# Revit family: 4_CFS494NVNA+TCF5841P+TES47MR+TH343R+HP430-7
name_source: partatom
category: 衛生器具
units: mm (PartAtom-declared; Revit-internal decimal feet)

## family parameters
OmniClass タイトル = Sanitary, Laundry, and Cleaning Equipment
OmniClass 番号 = 23.45.00.00
パーツ タイプ = 標準
ロード時にボイドで切り取り = はい
丸型コネクタ寸法 = 直径を使用
作業面ベース = いいえ
共有 = いいえ
常に垂直 = はい
部屋計算ポイント = いいえ

## types (1)
- CFS494NVNA+TCF5841P+TES47MR+TH343R+HP430-7
    3Dファイル形式 = rfa
    BLCJ仕様バージョン = Version1.0
    URL = https://jp.toto.com
    カウンター色 = <カテゴリ別>
    キーノート = 0表示の場合は商品仕様と設計数量をご確認ください
    データ作成ソフトVer = Revit ver.2019
    モデル = CFS494NVNA+TCF5841P+TES47MR+TH343R+HP430-7
    リモコン_位置切替 = いいえ
    リモコン_表示 = はい
    リモコン距離 = 600
    リモコン高さ = 850  [stored 2.78871 ft]
    ・右 = はい
    ・左 = いいえ
    上水負荷単位 = 0
    中水負荷単位 = 0
    付属単位 = TCF5841P+TES47MR+TH343R+HP430-7
    企業コード = 504860
    使用水 = 上水
    周波数 = 0 Hz
    商品情報URL = https://www.com-et.com
    商品紹介URL = https://jp.toto.com
    奥行 = 660
    幅 = 355
    排気配管 = はい
    排水接続口 = 75
    排水接続口情報 = VU、VP75塩ビ管
    排水芯・排水高さ = 255
    排水距離 = 255  [stored 0.836614 ft]
    排水配管 = はい
    最低使用圧力 = 0.1 MPa
    最高使用圧力 = 0.8 MPa
    極数 = 2
    構成品番 = CFS494NVNA+TCF5841P+TES47MR+TH343R+HP430-7
    水配管 = はい
    汚水負荷単位 = 0
    洗浄水量 = 4.8 L
    消耗品・備品情報 = Uﾊﾟｯｷﾝ：TH91938HP、シートパッキン：TH321、給水フィルター付水抜栓：TCM9032、脱臭フィルター：TCM9920、便座クッション：TCM1792R、便ふたクッション：TCM1794、脱臭カートリッジ：TCM11074
    消費電力 = 1260 W
    温水配管 = はい
    相 = 1
    給水接続口 = 25A
    給水接続口情報 = R1
    給水水平距離 = 180
    給水負荷単位(水栓) = 0
    給水負荷単位(洗浄) = 0
    給水距離 = 100  [stored 0.328084 ft]
    給湯負荷単位 = 0
    製品リリース年月 = 2023年8月
    製品出荷対象 = 国内
    製造元 = TOTO株式会社
    設置形態 = 床置
    説明 = パブリックコンパクト便器・フラッシュバルブ式_ウォシュレットアプリコットPAP2AK
    負荷分類 = 9_コンセント
    陶器色 = TOTO_#NW1 ホワイト
    雑排水負荷単位 = 0
    電圧 = 100 V
    電源_表示 = はい
    電源距離 = 370  [stored 1.21391 ft]
    電源高さ = 271

note: [stored X ft] marks values corroborated as IEEE doubles in the binary element streams (Revit-internal decimal feet)
